# Revit family: Furniture-Mirror_Cabinet-KOHLER-Elosis-K-15031T
name_source: partatom
category: Casework
units: mm (PartAtom-declared; Revit-internal decimal feet)

## family parameters
Cut with Voids When Loaded = No
Host = Face
OmniClass Number = 23.25.53.11.13.11
OmniClass Title = Medicine Cabinet
Room Calculation Point = No
Shared = No

## types (1)
- NA-Mild Silver
    ADA Compliant = No
    Assembly Code = E2010.30
    Construction Type = Wall Mount
    Date Modified = 08/01/2022
    Default Elevation = 60"
    Depth = 4 13/16"
    Description = Mirror Cabinet 508mm
    Finish = KOHLER-Metal-NA-Mild_Silver
    Hardware Included = No
    Height = 26 1/8"
    Manufacturer = Kohler Co.
    Master Format 2014 = 12 35 30.23
    Master Format 2014 Name = Bathroom Casework
    Material = Aluminium
    Model = K-15031T-NA
    Product Documentation Link = https://files.kohler.com.cn
    Product Finish = KOHLER-Metal-NA-Mild_Silver
    Product Name = Elosis
    Product Page URL = https://www.kohler.com.cn
    Type = 1
    URL = http://www.kohler.com.cn
    WaterSense Certified = No
    Width = 20"

## geometry (parser evidence)
native form markers: Sweep x6
no freeform markers — native parametric forms only
